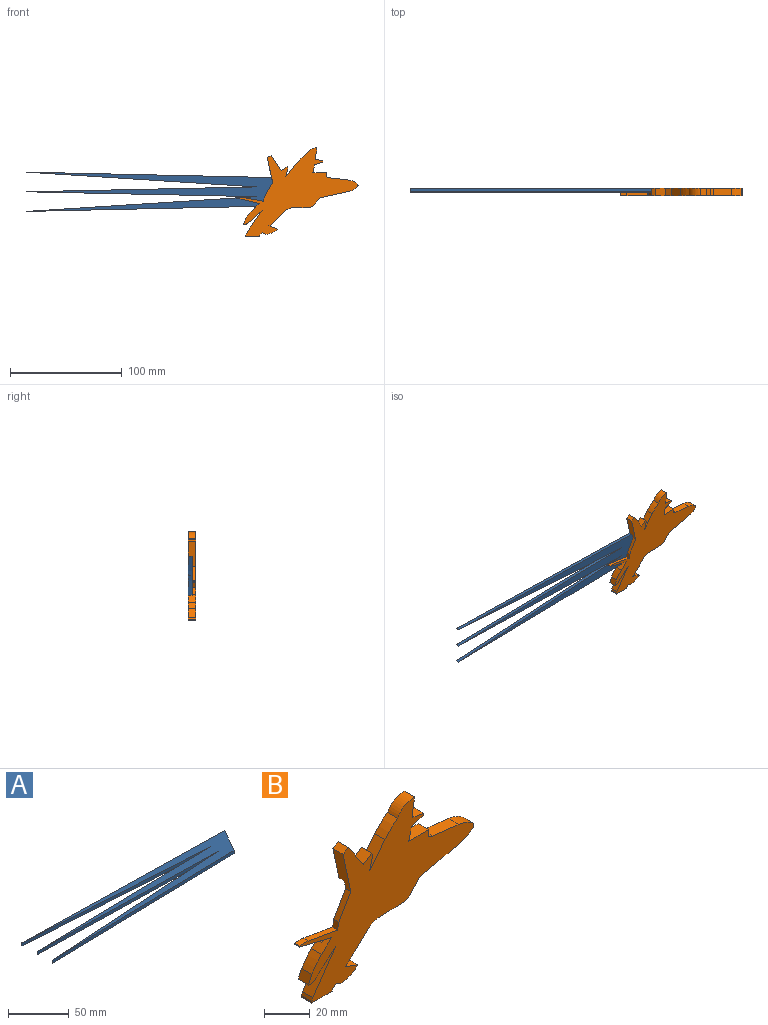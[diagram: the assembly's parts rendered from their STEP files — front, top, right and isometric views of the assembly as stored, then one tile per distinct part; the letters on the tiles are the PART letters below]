
ASSEMBLY  parts=2 mates=1
PART A: 9 faces, bbox 230.6x35.1x3.2 mm
  f0: plane 215.9x4.71mm, normal (0.02,-1,0), area 685.6mm2, adj f1,f6,f7,f8
  f1: plane 25.4x14.66mm, normal (0.87,-0.5,0), area 93.1mm2, adj f0,f2,f7,f8
  f2: plane 230.56x5.03mm, normal (0.02,1,0), area 732.2mm2, adj f1,f3,f7,f8
  f3: plane 206.38x13.21mm, normal (-0.06,-1,0), area 656.6mm2, adj f2,f4,f7,f8
  f4: plane 206.38x4.36mm, normal (-0.02,1,0), area 655.4mm2, adj f3,f5,f7,f8
  f5: plane 206.38x4.36mm, normal (-0.02,-1,0), area 655.4mm2, adj f4,f6,f7,f8
  f6: plane 206.38x13.21mm, normal (-0.06,1,0), area 656.6mm2, adj f0,f5,f7,f8
  f7: plane 230.56x35.14mm, normal (0,0,1), area 3132.4mm2, adj f0,f1,f2,f3,f4,f5,f6
  f8: plane 230.56x35.14mm, normal (0,0,-1), area 3132.4mm2, adj f0,f1,f2,f3,f4,f5,f6
PART B: 53 faces, bbox 108.3x6.4x79 mm
  f0: plane 12.7x7.33mm, normal (-0.87,0,0.5), area 46.6mm2, adj f1,f5,f44,f49
  f1: plane 3.97x3.18mm, normal (-0.98,0,0.21), area 12.9mm2, adj f0,f2,f44,f49
  f2: plane 18.38x3.23mm, normal (0.17,0,0.98), area 59.2mm2, adj f1,f3,f44,f49
  f3: plane 5.39x3.18mm, normal (0,0,1), area 17.1mm2, adj f2,f6,f44,f49
  f4: plane 20.01x4.95mm, normal (-0.24,0,-0.97), area 65.4mm2, adj f6,f7,f44,f49
  f5: plane 22.43x6.35mm, normal (-0.98,0,-0.21), area 130.4mm2, adj f0,f43,f44,f45,f46,f49
  f6: plane 3.18x0.53mm, normal (-1,0,0), area 1.7mm2, adj f3,f4,f44,f49
  f7: plane 6.35x6.26mm, normal (-0.68,0,0.73), area 42.3mm2, adj f4,f8,f44,f45,f48,f49
  f8: cylinder r=65.76mm len=7.68mm, axis (0,1,0), area 62.2mm2, adj f7,f9,f44,f45
  f9: plane 6.35x4.79mm, normal (-0.92,0,0.38), area 32.9mm2, adj f8,f10,f44,f45
  f10: cylinder r=2.99mm len=6.35mm, axis (0,1,0), area 22.5mm2, adj f9,f11,f44,f45
  f11: plane 13.54x12.02mm, normal (0.66,0,-0.75), area 115mm2, adj f10,f12,f44,f45
  f12: plane 20.56x14.2mm, normal (-0.82,0,0.57), area 158.7mm2, adj f11,f13,f44,f45
  f13: plane 6.35x1.77mm, normal (-0.93,0,0.37), area 12.1mm2, adj f12,f44,f45,f50
  f14: plane 6.35x2.53mm, normal (0.67,0,-0.74), area 21.7mm2, adj f15,f44,f45,f51
  f15: plane 6.35x2.76mm, normal (-0.47,0,-0.88), area 19.8mm2, adj f14,f16,f44,f45
  f16: cylinder r=15.29mm len=10.74mm, axis (0,1,0), area 76.1mm2, adj f15,f17,f44,f45
  f17: plane 7.71x6.35mm, normal (0.35,0,0.94), area 52.2mm2, adj f16,f18,f44,f45
  f18: plane 13.89x13.11mm, normal (0.69,0,-0.73), area 121.3mm2, adj f17,f19,f44,f45
  f19: cylinder r=11.35mm len=6.51mm, axis (0,1,0), area 46.4mm2, adj f18,f20,f44,f45
  f20: plane 15.54x6.35mm, normal (0.03,0,-1), area 98.7mm2, adj f19,f21,f44,f45
  f21: cylinder r=5.89mm len=6.35mm, axis (0,1,0), area 30.7mm2, adj f20,f22,f44,f45
  f22: plane 6.58x6.35mm, normal (0.75,0,-0.66), area 55.4mm2, adj f21,f23,f44,f45
  f23: plane 26.02x6.35mm, normal (0.22,0,-0.98), area 169.4mm2, adj f22,f24,f44,f45
  f24: cylinder r=12.83mm len=7.43mm, axis (0,1,0), area 55.6mm2, adj f23,f25,f44,f45
  f25: cylinder r=1.87mm len=6.35mm, axis (0,1,0), area 13.4mm2, adj f24,f26,f44,f45
  f26: cylinder r=16.41mm len=8.84mm, axis (0,1,0), area 62.2mm2, adj f25,f27,f44,f45
  f27: plane 16.29x6.35mm, normal (0.11,0,0.99), area 104.1mm2, adj f26,f28,f44,f45
  f28: plane 6.35x2.69mm, normal (0.34,0,0.94), area 18.2mm2, adj f27,f29,f44,f45
  f29: plane 6.35x3.92mm, normal (1,0,0.03), area 24.9mm2, adj f28,f30,f44,f45
  f30: plane 12.11x6.35mm, normal (-0.03,0,1), area 76.9mm2, adj f29,f31,f44,f45
  f31: plane 7.14x6.35mm, normal (0.98,0,-0.22), area 46.5mm2, adj f30,f32,f44,f45
  f32: plane 7.38x6.35mm, normal (0.31,0,-0.95), area 49.4mm2, adj f31,f33,f44,f45
  f33: plane 6.35x1.2mm, normal (1,0,0), area 7.6mm2, adj f32,f34,f44,f45
  f34: plane 7.02x6.35mm, normal (0.16,0,0.99), area 45.1mm2, adj f33,f35,f44,f45
  f35: plane 10.37x6.35mm, normal (0.99,0,-0.16), area 66.7mm2, adj f34,f36,f44,f45
  f36: cylinder r=11.74mm len=10.45mm, axis (0,1,0), area 81.2mm2, adj f35,f37,f44,f45
  f37: cylinder r=36.58mm len=7.95mm, axis (0,1,0), area 69.5mm2, adj f36,f38,f44,f45
  f38: plane 12.09x9.52mm, normal (-0.79,0,0.62), area 97.7mm2, adj f37,f39,f44,f45
  f39: plane 7.86x6.35mm, normal (0.97,0,-0.24), area 51.4mm2, adj f38,f40,f44,f45
  f40: plane 6.35x1.06mm, normal (0.84,0,0.55), area 8.1mm2, adj f39,f41,f44,f45
  f41: plane 6.35x5.35mm, normal (-0.55,0,0.84), area 40.7mm2, adj f40,f42,f44,f45
  f42: plane 13.53x8.9mm, normal (0.84,0,0.55), area 102.8mm2, adj f41,f43,f44,f45
  f43: plane 6.35x3.55mm, normal (-0.45,0,0.89), area 25.2mm2, adj f5,f42,f44,f45
  f44: plane 108.33x78.97mm, normal (0,-1,0), area 3003.9mm2, adj f0,f1,f2,f3,f4,f5,f6,f7
  f45: plane 102.64x78.97mm, normal (0,1,0), area 2757mm2, adj f5,f7,f8,f9,f10,f11,f12,f13
  f46: plane 10.96x3.18mm, normal (-0.02,0,-1), area 34.8mm2, adj f5,f45,f47,f49
  f47: plane 25.8x14.89mm, normal (-0.87,0,0.5), area 94.6mm2, adj f45,f46,f48,f49
  f48: plane 9.79x3.18mm, normal (-0.03,0,1), area 31.1mm2, adj f7,f45,f47,f49
  f49: plane 41.9x26.24mm, normal (0,1,0), area 246.8mm2, adj f0,f1,f2,f3,f4,f5,f6,f7
  f50: plane 6.35x0.79mm, normal (-1,0,0), area 5mm2, adj f13,f44,f45,f52
  f51: plane 6.35x0.79mm, normal (1,0,0), area 5mm2, adj f14,f44,f45,f52
  f52: plane 12.7x6.35mm, normal (0,0,-1), area 80.6mm2, adj f44,f45,f50,f51
PLACE A rot(axis=(1,0,0),90deg) t=(-18.59,2.46,0.18)mm
PLACE B t=(3.32,4.05,2.31)mm
MATE fastened A.f1 <-> B.f47  axis (0.87,0,-0.5) through (-18.69,2.46,0.02)mm
